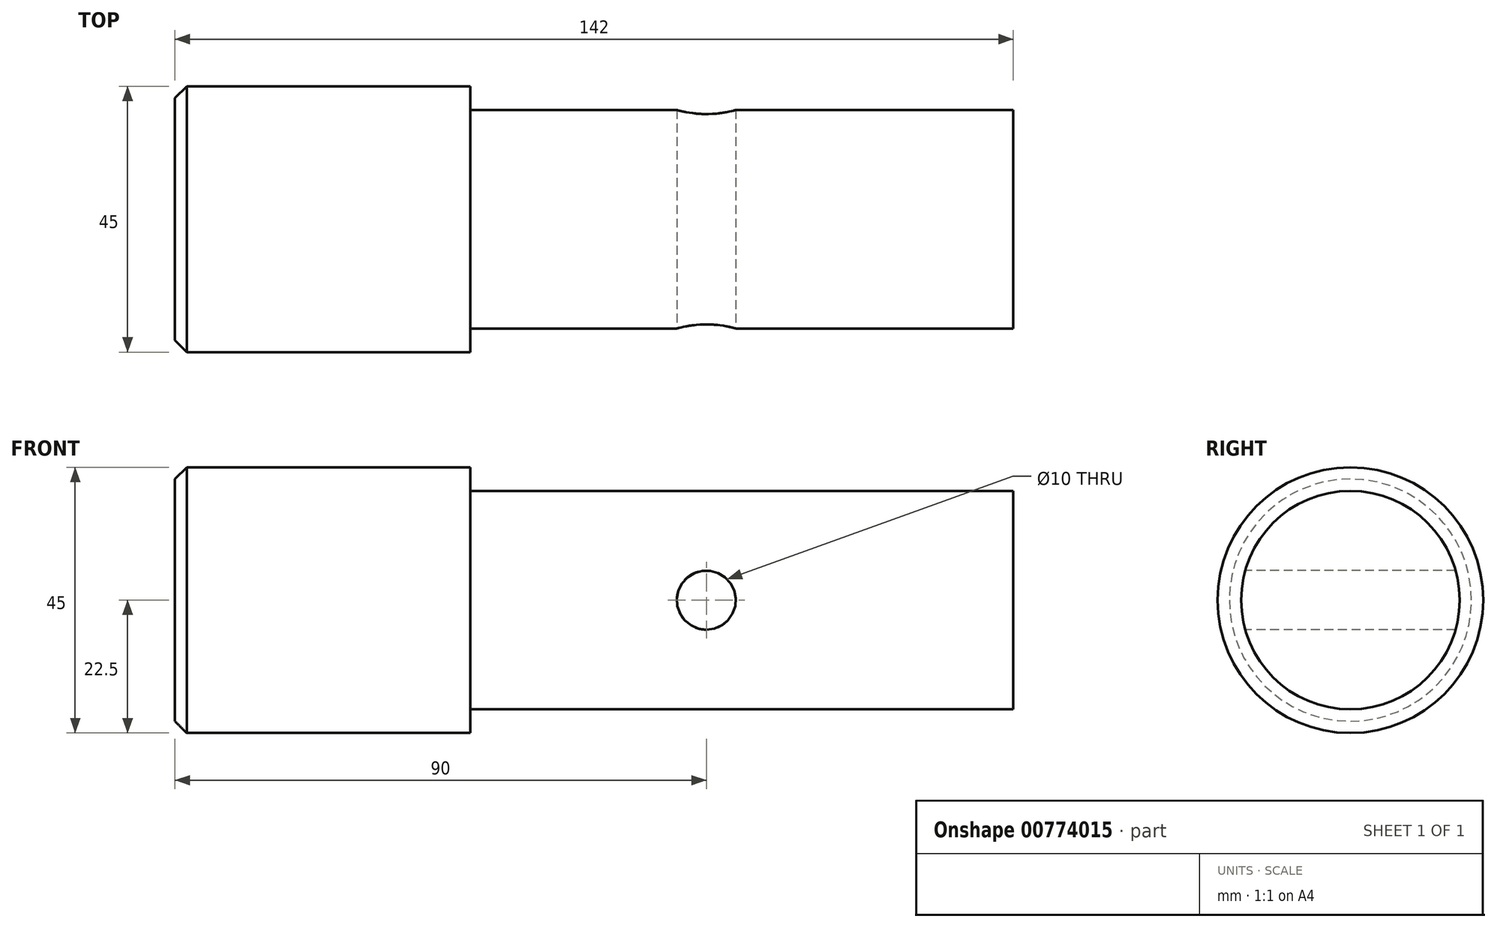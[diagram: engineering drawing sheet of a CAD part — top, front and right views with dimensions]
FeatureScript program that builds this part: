
annotation { "Feature Type Name" : "Feature", "Feature Type Description" : "" }
export const myFeature = defineFeature(function(context is Context, id is Id, definition is map)
    precondition{}
    {
        {
            var Q0;
            Q0=qCreatedBy(makeId("Right.planeOp"),FACE);
            var sketch = newSketch(context, id + "F0", { "sketchPlane" : qUnion([Q0])});
            skCircle(sketch, "E0", {"center": v(0, 0) * mm, "radius": 22.5 * mm});
            skCircle(sketch, "E1", {"center": v(0, 0) * mm, "radius": 18.5 * mm});
            skSolve(sketch);
        }
        {
            var Q0;
            Q0=makeQuery(id+"F0.imprint","IMPRINT",FACE,{"disambiguationData":[TD([[makeQuery(id+"F0.imprint","IMPRINT",EDGE,{"derivedFrom":sQuery(id+"F0.wireOp",EDGE,"E1")}),1.0]])]});
            extrude(context, id + "F1", {"entities" : qUnion([Q0]), "depth" : 142 * mm, "offsetDistance" : 25 * mm});
        }
        {
            var Q0;
            Q0 = qSketchRegion(id + "F0", true);
            extrude(context, id + "F2", {"entities" : qUnion([Q0]), "operationType" : NewBodyOperationType.ADD, "depth" : (142 - 92) * mm, "offsetDistance" : 25 * mm});
        }
        {
            var Q0;
            Q0=makeQuery(id+"F2.opExtrude","CAP_EDGE",EDGE,{"disambiguationData":[OSD([sQuery(id+"F0.wireOp",EDGE,"E0")])],"isStart":true});
            chamfer(context, id + "F3", {"entities" : qUnion([Q0]), "width" : 2 * mm, "tangentPropagation" : true});
        }
        {
            var Q0;
            Q0=makeQuery(id+"F1.opExtrude","SWEPT_FACE",FACE,{"disambiguationData":[OSD([sQuery(id+"F0.wireOp",EDGE,"E1")])]});
            cPlane(context, id + "F4", {"entities" : qUnion([Q0]), "cplaneType" : CPlaneType.LINE_ANGLE, "offset" : 25 * mm, "angle" : 0 * degree, "width" : 150 * mm, "height" : 150 * mm});
        }
        {
            var Q0;
            Q0=qCreatedBy(id+"F4.planeOp",FACE);
            var sketch = newSketch(context, id + "F5", { "sketchPlane" : qUnion([Q0])});
            skLineSegment(sketch, "E2", {"start": v(142, 0) * mm, "end": v(90, 0) * mm, "construction": true});
            skCircle(sketch, "E3", {"center": v(90, 0) * mm, "radius": 5 * mm});
            skSolve(sketch);
        }
        {
            var Q0;
            Q0 = qSketchRegion(id + "F5", true);
            extrude(context, id + "F6", {"entities" : qUnion([Q0]), "operationType" : NewBodyOperationType.REMOVE, "oppositeDirection" : true, "depth" : 100 * mm, "offsetDistance" : 25 * mm, "symmetric" : true});
        }
    });
